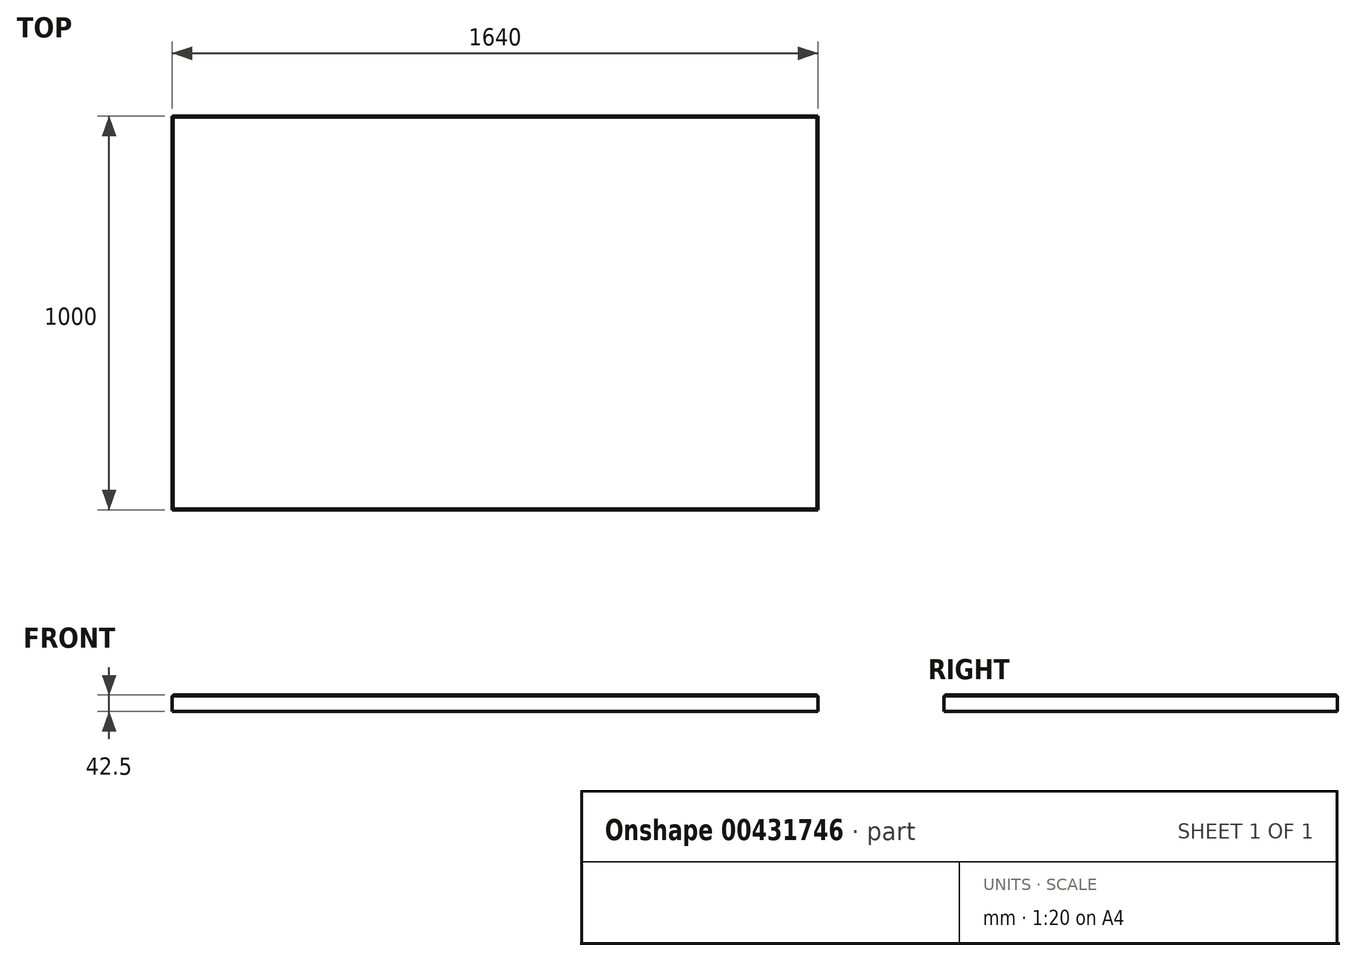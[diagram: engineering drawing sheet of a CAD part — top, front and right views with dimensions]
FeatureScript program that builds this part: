
annotation { "Feature Type Name" : "Feature", "Feature Type Description" : "" }
export const myFeature = defineFeature(function(context is Context, id is Id, definition is map)
    precondition{}
    {
        {
            var Q0;
            Q0=qCreatedBy(makeId("Top.planeOp"),FACE);
            var sketch = newSketch(context, id + "F0", { "sketchPlane" : qUnion([Q0])});
            skLineSegment(sketch, "E0.bottom", {"start": v(820, -500) * mm, "end": v(-820, -500) * mm});
            skLineSegment(sketch, "E0.top", {"start": v(820, 500) * mm, "end": v(-820, 500) * mm});
            skLineSegment(sketch, "E0.left", {"start": v(820, -500) * mm, "end": v(820, 500) * mm});
            skLineSegment(sketch, "E0.right", {"start": v(-820, -500) * mm, "end": v(-820, 500) * mm});
            skPoint(sketch, "E0.middle", {"position": v(0, 0) * mm});
            skSolve(sketch);
        }
        {
            var Q0;
            Q0=makeQuery(id+"F0.imprint","IMPRINT",FACE,{"disambiguationData":[TD([[makeQuery(id+"F0.imprint","IMPRINT",EDGE,{"derivedFrom":sQuery(id+"F0.wireOp",EDGE,"E0.bottom")}),-1.0]])]});
            extrude(context, id + "F1", {"entities" : qUnion([Q0]), "depth" : 40 * mm});
        }
        {
            var Q0;
            Q0=makeQuery(id+"F1.opExtrude","CAP_FACE",FACE,{"disambiguationData":[OSD([sQuery(id+"F0.wireOp",EDGE,"E0.bottom"),sQuery(id+"F0.wireOp",EDGE,"E0.top"),sQuery(id+"F0.wireOp",EDGE,"E0.left"),sQuery(id+"F0.wireOp",EDGE,"E0.right")])],"isStart":false});
            shell(context, id + "F2", {"entities" : qUnion([Q0]), "thickness" : 2.5 * mm});
        }
        {
            var Q0;
            Q0=makeQuery(id+"F2.opShell","OFFSET_FACE",FACE,{"disambiguationData":[OSD([sQuery(id+"F0.wireOp",EDGE,"E0.bottom"),sQuery(id+"F0.wireOp",EDGE,"E0.top"),sQuery(id+"F0.wireOp",EDGE,"E0.left"),sQuery(id+"F0.wireOp",EDGE,"E0.right")])]});
            extrude(context, id + "F3", {"entities" : qUnion([Q0]), "operationType" : NewBodyOperationType.ADD, "depth" : 40 * mm});
        }
    });
